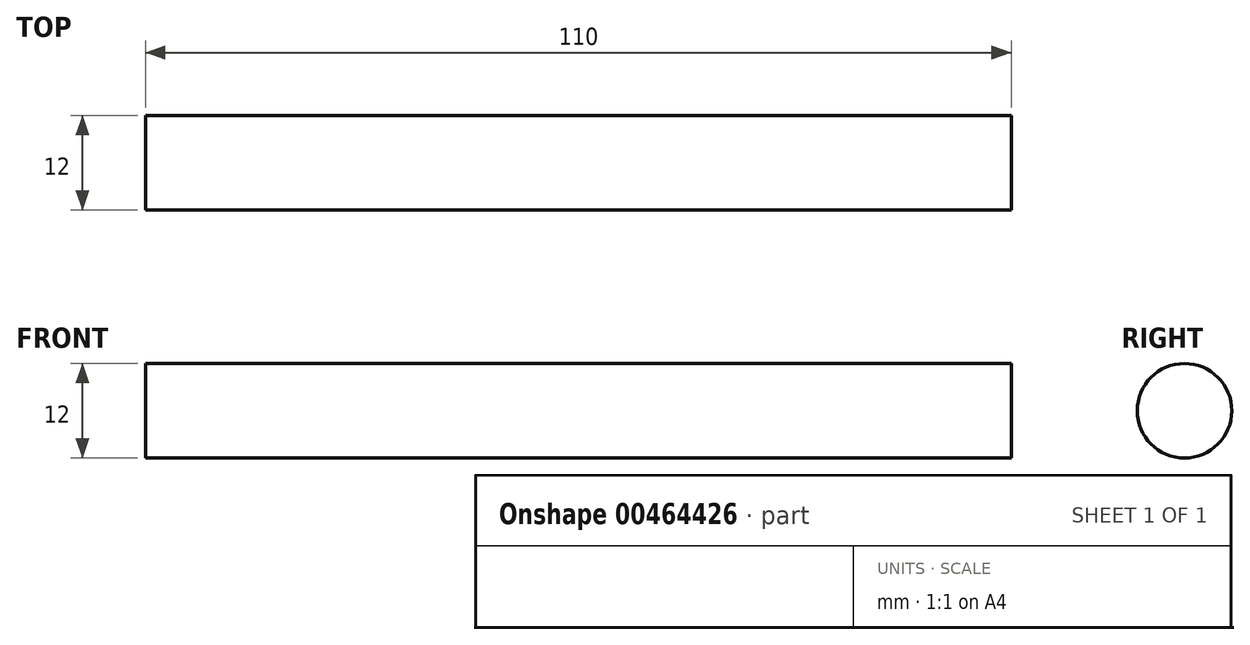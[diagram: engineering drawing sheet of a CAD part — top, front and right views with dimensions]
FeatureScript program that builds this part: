
annotation { "Feature Type Name" : "Feature", "Feature Type Description" : "" }
export const myFeature = defineFeature(function(context is Context, id is Id, definition is map)
    precondition{}
    {
        {
            var Q0;
            Q0=qCreatedBy(makeId("Front.planeOp"),FACE);
            var sketch = newSketch(context, id + "F0", { "sketchPlane" : qUnion([Q0])});
            skLineSegment(sketch, "E0.bottom", {"start": v(0, 0) * mm, "end": v(-55, 0) * mm});
            skLineSegment(sketch, "E0.top", {"start": v(0, 6) * mm, "end": v(-55, 6) * mm});
            skLineSegment(sketch, "E0.left", {"start": v(0, 0) * mm, "end": v(0, 6) * mm});
            skLineSegment(sketch, "E0.right", {"start": v(-55, 0) * mm, "end": v(-55, 6) * mm});
            skLineSegment(sketch, "E1.MirrorCS", {"start": v(0, 6) * mm, "end": v(55, 6) * mm});
            skLineSegment(sketch, "E2.MirrorCS", {"start": v(55, 0) * mm, "end": v(55, 6) * mm});
            skLineSegment(sketch, "E3.MirrorCS", {"start": v(0, 0) * mm, "end": v(55, 0) * mm});
            skSolve(sketch);
        }
        {
            var Q0;
            Q0=qSketchRegion(id+"F0",true);
            var Q1;
            Q1=sQuery(id+"F0.wireOp",EDGE,"E0.bottom");
            revolve(context, id + "F1", {"entities" : qUnion([Q0]), "axis" : qUnion([Q1]), "revolveType" : RevolveType.FULL});
        }
    });
